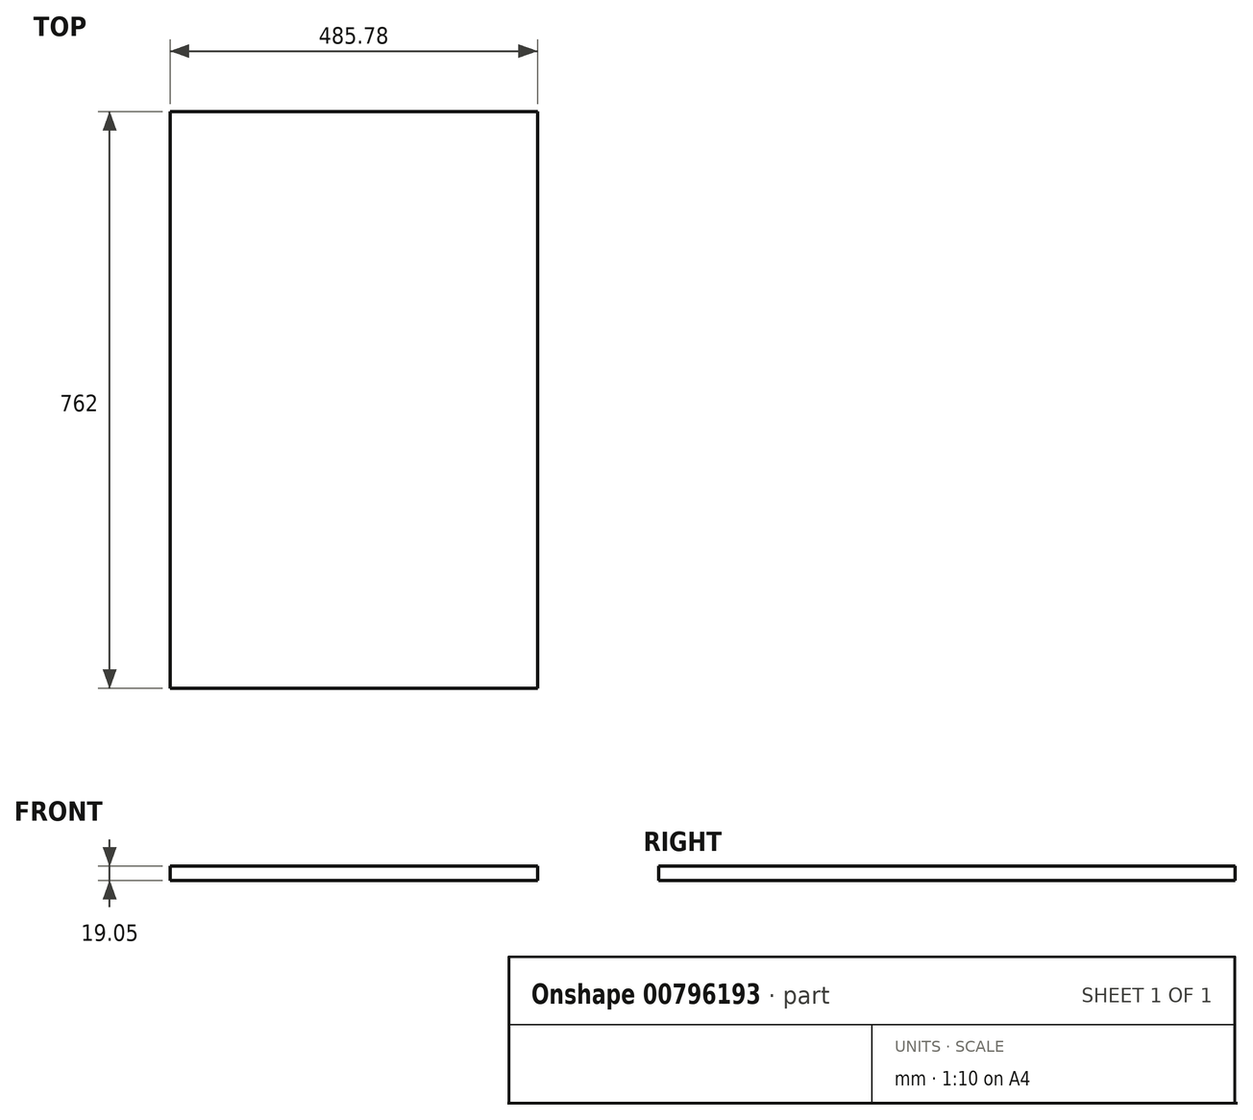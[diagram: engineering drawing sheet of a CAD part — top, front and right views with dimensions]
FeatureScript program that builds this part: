
annotation { "Feature Type Name" : "Feature", "Feature Type Description" : "" }
export const myFeature = defineFeature(function(context is Context, id is Id, definition is map)
    precondition{}
    {
        {
            var Q0;
            Q0=qCreatedBy(makeId("Top.planeOp"),FACE);
            var sketch = newSketch(context, id + "F0", { "sketchPlane" : qUnion([Q0])});
            skLineSegment(sketch, "E0.bottom", {"start": v(-242.89, 381) * mm, "end": v(242.89, 381) * mm});
            skLineSegment(sketch, "E0.top", {"start": v(-242.89, -381) * mm, "end": v(242.89, -381) * mm});
            skLineSegment(sketch, "E0.left", {"start": v(-242.89, 381) * mm, "end": v(-242.89, -381) * mm});
            skLineSegment(sketch, "E0.right", {"start": v(242.89, 381) * mm, "end": v(242.89, -381) * mm});
            skPoint(sketch, "E0.middle", {"position": v(0, 0) * mm});
            skSolve(sketch);
        }
        {
            var Q0;
            Q0 = qSketchRegion(id + "F0", true);
            extrude(context, id + "F1", {"entities" : qUnion([Q0]), "depth" : 19.05 * mm, "offsetDistance" : 25.4 * mm});
        }
    });
